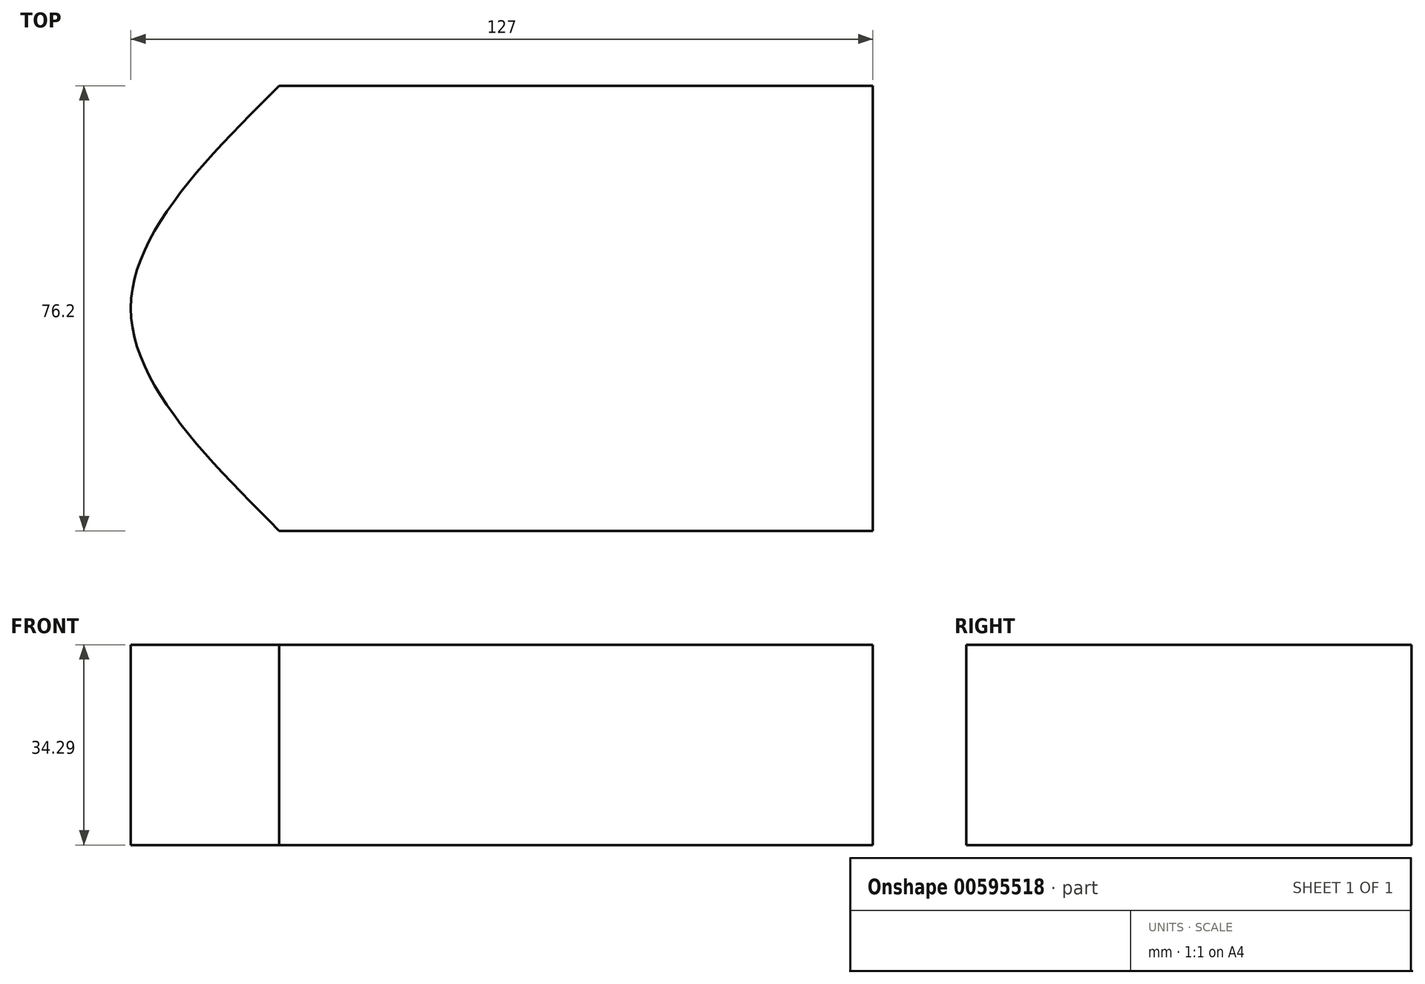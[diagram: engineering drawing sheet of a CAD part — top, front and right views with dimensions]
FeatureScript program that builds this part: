
annotation { "Feature Type Name" : "Feature", "Feature Type Description" : "" }
export const myFeature = defineFeature(function(context is Context, id is Id, definition is map)
    precondition{}
    {
        {
            var Q0;
            Q0=qCreatedBy(makeId("Top.planeOp"),FACE);
            var sketch = newSketch(context, id + "F0", { "sketchPlane" : qUnion([Q0])});
            skLineSegment(sketch, "E0.bottom", {"start": v(50.8, -38.1) * mm, "end": v(-50.8, -38.1) * mm});
            skLineSegment(sketch, "E0.top", {"start": v(50.8, 38.1) * mm, "end": v(-50.8, 38.1) * mm});
            skLineSegment(sketch, "E0.left", {"start": v(50.8, -38.1) * mm, "end": v(50.8, 38.1) * mm});
            skLineSegment(sketch, "E0.right", {"start": v(-50.8, -38.1) * mm, "end": v(-50.8, 38.1) * mm});
            skPoint(sketch, "E0.middle", {"position": v(0, 0) * mm});
            skLineSegment(sketch, "E1", {"start": v(50.8, 0) * mm, "end": v(-76.2, 0) * mm});
            skPoint(sketch, "E1.endSnap0", {"position": v(50.8, 0) * mm});
            skFitSpline(sketch, "E2", {"points": [v(-50.8, 38.1) * mm, v(-76.2, 0) * mm, v(-50.8, -38.1) * mm], "startDerivative": vector(-76.2, -76.2) * mm, "endDerivative": vector(76.2, -76.2) * mm});
            skSolve(sketch);
        }
        {
            var Q0;
            Q0 = qSketchRegion(id + "F0", true);
            extrude(context, id + "F1", {"entities" : qUnion([Q0]), "depth" : 34.3 * mm, "offsetDistance" : 25.4 * mm});
        }
    });
